# Revit family: IS_TonicII_A6336_BIM_GB
name_source: partatom
category: Plumbing Fixtures
revit_build: Autodesk Revit MEP 2012 (Build: 20110309_2315(x64)
units: mm (PartAtom-declared; Revit-internal decimal feet)

## types (1)
- A6336AA-TONIC II SL Bidet mixer with PUW
    AreaUnits = millimeters
    Assembly Code = C1030200
    AssetType = Fixed
    BIMObjectName = ISI_IdealStandard_BidetTaps_TonicII_A6336
    BarCode = 4015413335041
    Brand = Ideal Standard
    ConnectionType = Plumbing
    Default Elevation = 1219 mm
    Description = Tonic ii single lever one hole bidet mixer with pop-up waste
    DurationUnit = year
    ECA = No
    ExpectedLife = 30
    FaucetFunction = MIXED
    FaucetOperation = Other
    FaucetTopDescription = Lever
    FaucetType = Other
    Features = Single lever one hole bidet mixer with pop-up waste
    Finish = Chrome
    IfcExportAs = IfcValveType
    IfcExportType = FAUCET
    InstallationDate = 1900-12-31T23:59:59
    InstallationInstructions = www.idealspec.co.uk/resources.html
    LinearUnits = millimeters
    ManufacturerURL = www.idealspec.co.uk
    Model = A6336AA
    ModelNumber = A6336AA
    ModelReference = Tonic ii single lever one hole bidet mixer with pop-up waste
    NBSDescription = Water supply fittings for bidets
    NBSReference = 45-35-70/323
    Name = BidetTaps_TonicII_A6336_IdealStandard
    NettWeight = 1.67 Kg
    NominalDepth = 148 mm
    NominalHeight = 137 mm
    NominalLength = 148 mm
    NominalWidth = 51 mm
    ProductInformation = www.idealspec.co.uk/assets/datasheet/A6336AA
    Shape = Sculptured
    Size = 137 x 148 x 51 mm
    Space = Internal
    SpareParts = www.fastpart-spares.co.uk
    SustainabilityPerformance = Can be recycled
    TestPressure = 10 Bar
    URL = www.idealspec.co.uk
    Uniclass2 = Pr_40_20_87_11
    Version = 1
    VolumeUnits = Litres
    WRAS = No
    WarrantyDescription = Manufacturers warranty
    WarrantyDurationParts = 5
    WarrantyDurationUnit = year
    WarrantyStartDate = 1900-12-31T23:59:59
    WaterEfficientProduct = No
    WorkingPressure = 5 L/min @ 3 bar

## geometry (parser evidence)
native form markers: Sweep x2
no freeform markers — native parametric forms only
